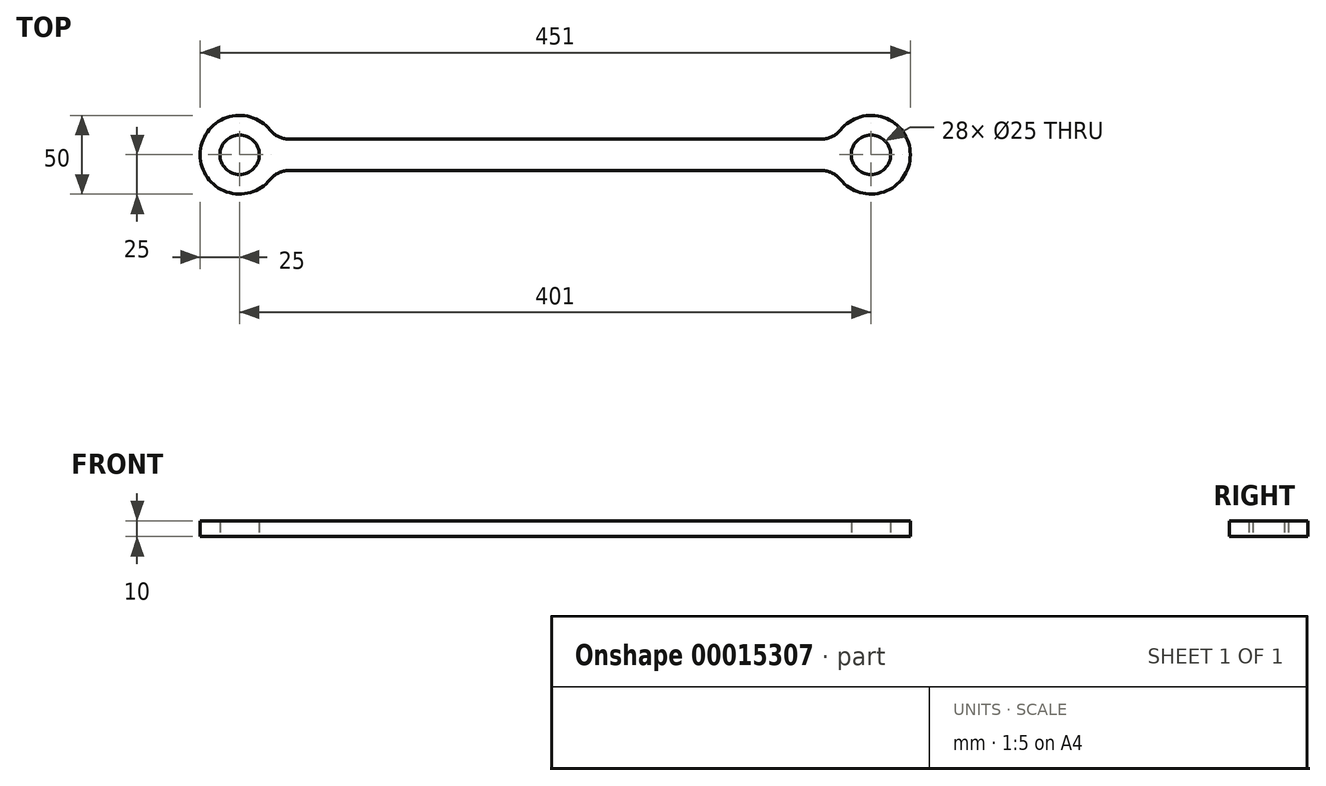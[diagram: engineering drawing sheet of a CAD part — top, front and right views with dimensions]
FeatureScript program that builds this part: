
annotation { "Feature Type Name" : "Feature", "Feature Type Description" : "" }
export const myFeature = defineFeature(function(context is Context, id is Id, definition is map)
    precondition{}
    {
        {
            var Q0;
            Q0=qCreatedBy(makeId("Top.planeOp"),FACE);
            var sketch = newSketch(context, id + "F0", { "sketchPlane" : qUnion([Q0])});
            skArc(sketch, "E0", {"start": v(19.52, 15.63) * mm, "mid": v(-25, 0) * mm, "end": v(19.52, -15.63) * mm});
            skArc(sketch, "E1", {"start": v(381.48, -15.63) * mm, "mid": v(426, 0) * mm, "end": v(381.48, 15.63) * mm});
            skLineSegment(sketch, "E2", {"start": v(31.22, 10) * mm, "end": v(369.78, 10) * mm});
            skLineSegment(sketch, "E3", {"start": v(0, 0) * mm, "end": v(401, 0) * mm, "construction": true});
            skLineSegment(sketch, "E4.MirrorCS", {"start": v(31.22, -10) * mm, "end": v(369.78, -10) * mm});
            skPoint(sketch, "E5.visualSharp", {"position": v(22.91, 10) * mm});
            skArc(sketch, "E5.filletArc", {"start": v(19.52, 15.62) * mm, "mid": v(24.73, 11.48) * mm, "end": v(31.22, 10) * mm});
            skPoint(sketch, "E6.visualSharp", {"position": v(22.91, -10) * mm});
            skArc(sketch, "E6.filletArc", {"start": v(31.22, -10) * mm, "mid": v(24.73, -11.48) * mm, "end": v(19.52, -15.62) * mm});
            skPoint(sketch, "E7.visualSharp", {"position": v(378.09, -10) * mm});
            skArc(sketch, "E7.filletArc", {"start": v(381.48, -15.63) * mm, "mid": v(376.27, -11.48) * mm, "end": v(369.78, -10) * mm});
            skPoint(sketch, "E8.visualSharp", {"position": v(378.09, 10) * mm});
            skArc(sketch, "E8.filletArc", {"start": v(369.78, 10) * mm, "mid": v(376.27, 11.48) * mm, "end": v(381.48, 15.63) * mm});
            skCircle(sketch, "E9", {"center": v(0, 0) * mm, "radius": 12.5 * mm});
            skCircle(sketch, "E10", {"center": v(401, 0) * mm, "radius": 12.5 * mm});
            skSolve(sketch);
        }
        {
            var Q0;
            Q0=qSketchRegion(id+"F0",true);
            extrude(context, id + "F1", {"entities" : qUnion([Q0]), "depth" : 10 * mm});
        }
    });
